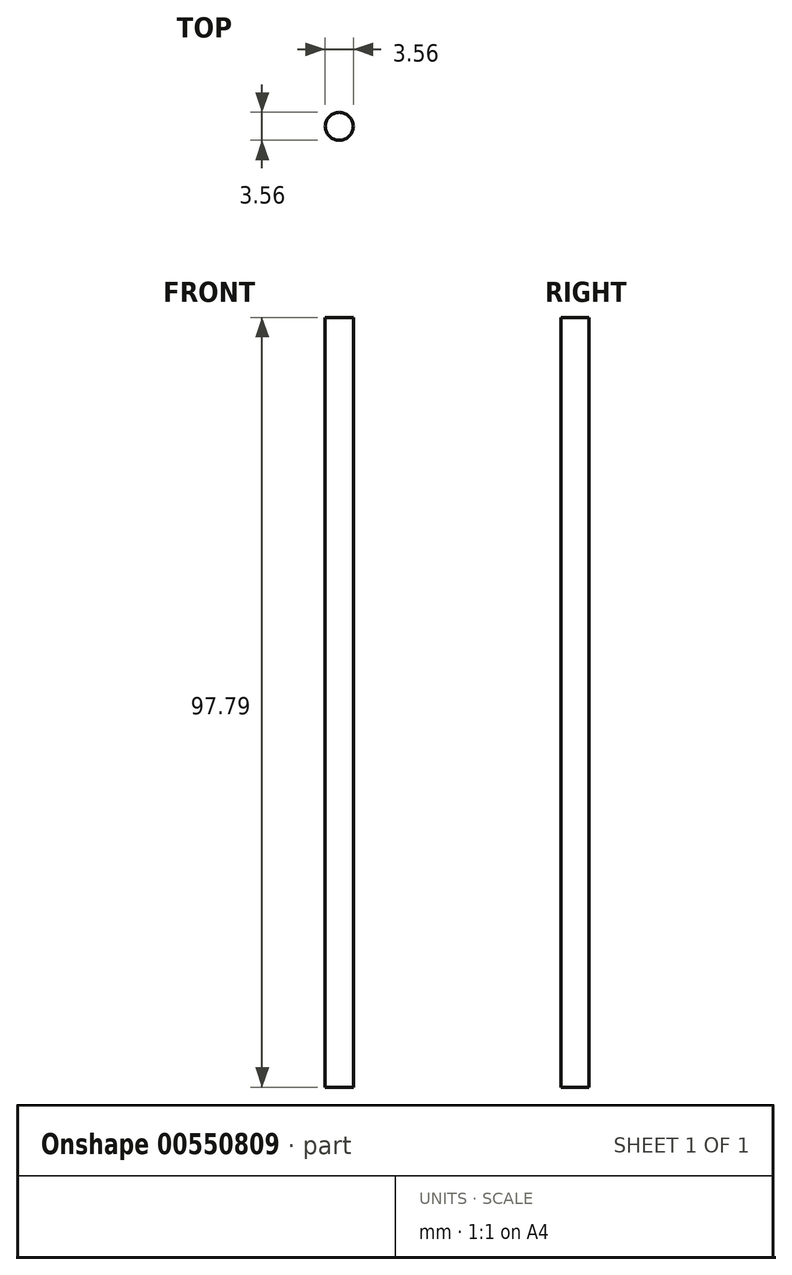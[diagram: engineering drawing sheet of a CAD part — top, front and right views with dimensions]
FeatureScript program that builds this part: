
annotation { "Feature Type Name" : "Feature", "Feature Type Description" : "" }
export const myFeature = defineFeature(function(context is Context, id is Id, definition is map)
    precondition{}
    {
        {
            var Q0;
            Q0=qCreatedBy(makeId("Top.planeOp"),FACE);
            var sketch = newSketch(context, id + "F0", { "sketchPlane" : qUnion([Q0])});
            skCircle(sketch, "E0", {"center": v(0, 0) * mm, "radius": 1.78 * mm});
            skSolve(sketch);
        }
        {
            var Q0;
            Q0=makeQuery(id+"F0.imprint","IMPRINT",FACE,{"disambiguationData":[TD([[makeQuery(id+"F0.imprint","IMPRINT",EDGE,{"derivedFrom":sQuery(id+"F0.wireOp",EDGE,"E0")}),1.0]])]});
            extrude(context, id + "F1", {"entities" : qUnion([Q0]), "depth" : 97.8 * mm, "offsetDistance" : 25.4 * mm});
        }
    });
